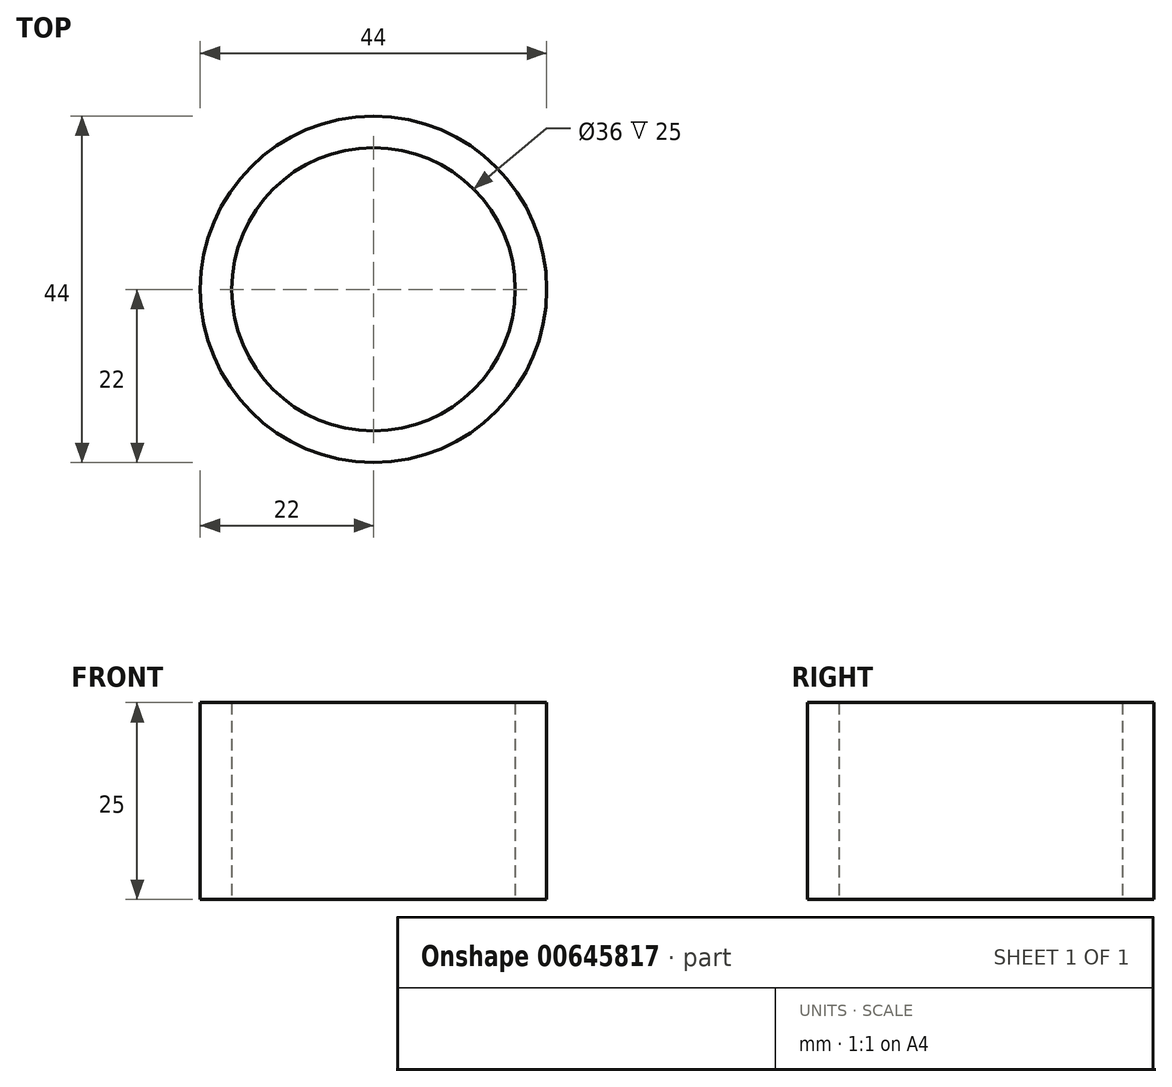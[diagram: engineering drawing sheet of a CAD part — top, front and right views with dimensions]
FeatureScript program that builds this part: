
annotation { "Feature Type Name" : "Feature", "Feature Type Description" : "" }
export const myFeature = defineFeature(function(context is Context, id is Id, definition is map)
    precondition{}
    {
        {
            var Q0;
            Q0=qCreatedBy(makeId("Top.planeOp"),FACE);
            var sketch = newSketch(context, id + "F0", { "sketchPlane" : qUnion([Q0])});
            skCircle(sketch, "E0", {"center": v(0, 0) * mm, "radius": 18 * mm});
            skCircle(sketch, "E1", {"center": v(0, 0) * mm, "radius": 22 * mm});
            skSolve(sketch);
        }
        {
            var Q0;
            Q0 = qSketchRegion(id + "F0", true);
            extrude(context, id + "F1", {"entities" : qUnion([Q0]), "depth" : 25 * mm, "offsetDistance" : 25 * mm});
        }
    });
